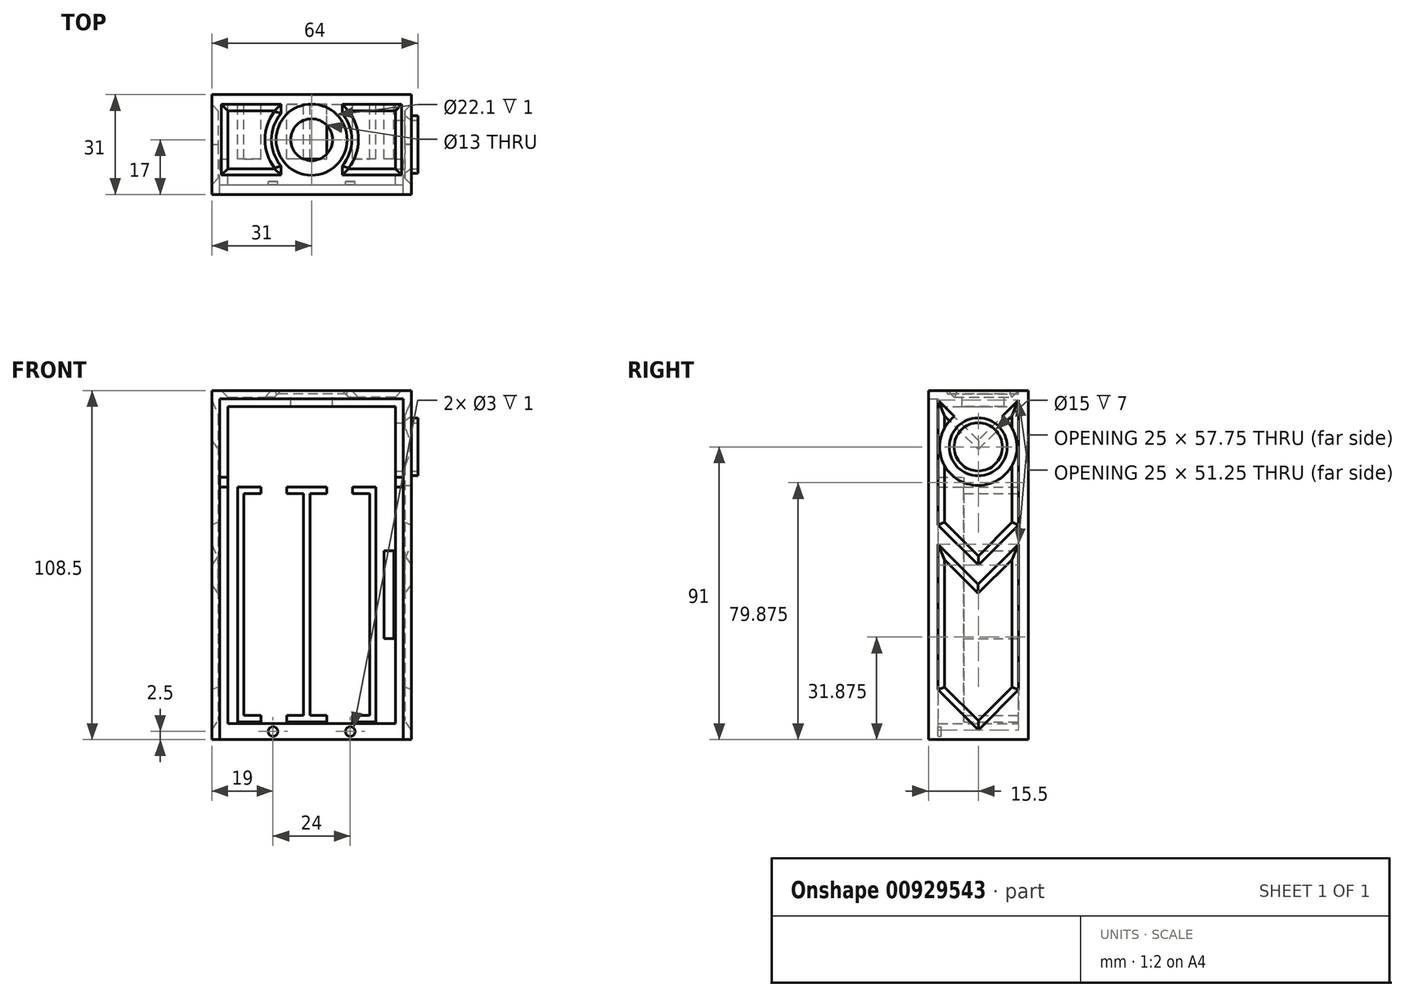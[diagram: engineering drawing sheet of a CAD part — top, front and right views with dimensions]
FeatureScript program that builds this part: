
annotation { "Feature Type Name" : "Feature", "Feature Type Description" : "" }
export const myFeature = defineFeature(function(context is Context, id is Id, definition is map)
    precondition{}
    {
        {
            var Q0;
            Q0=qCreatedBy(makeId("Front.planeOp"),FACE);
            var sketch = newSketch(context, id + "F0", { "sketchPlane" : qUnion([Q0])});
            skLineSegment(sketch, "E0.bottom", {"start": v(21.5, -36.5) * mm, "end": v(14.25, -36.5) * mm});
            skLineSegment(sketch, "E0.top", {"start": v(21.5, 36.5) * mm, "end": v(14.25, 36.5) * mm});
            skLineSegment(sketch, "E0.left", {"start": v(21.5, -36.5) * mm, "end": v(21.5, 36.5) * mm});
            skLineSegment(sketch, "E0.right", {"start": v(-21.5, -36.5) * mm, "end": v(-21.5, 36.5) * mm});
            skPoint(sketch, "E0.middle", {"position": v(0, 0) * mm});
            skLineSegment(sketch, "E1.bottom", {"start": v(-19.5, 34.5) * mm, "end": v(-14.25, 34.5) * mm});
            skLineSegment(sketch, "E1.top", {"start": v(-19.5, -34.5) * mm, "end": v(-14.25, -34.5) * mm});
            skLineSegment(sketch, "E1.left", {"start": v(-19.5, 34.5) * mm, "end": v(-19.5, -34.5) * mm});
            skLineSegment(sketch, "E1.right", {"start": v(-1, 34.5) * mm, "end": v(-1, -34.5) * mm});
            skLineSegment(sketch, "E2.bottom", {"start": v(1, 34.5) * mm, "end": v(6.25, 34.5) * mm});
            skLineSegment(sketch, "E2.top", {"start": v(1, -34.5) * mm, "end": v(6.25, -34.5) * mm});
            skLineSegment(sketch, "E2.left", {"start": v(1, 34.5) * mm, "end": v(1, -34.5) * mm});
            skLineSegment(sketch, "E2.right", {"start": v(19.5, 34.5) * mm, "end": v(19.5, -34.5) * mm});
            skLineSegment(sketch, "E3", {"start": v(-14.25, 34.5) * mm, "end": v(-14.25, 36.5) * mm});
            skLineSegment(sketch, "E4", {"start": v(-6.25, 34.5) * mm, "end": v(-6.25, 36.5) * mm});
            skLineSegment(sketch, "E5", {"start": v(6.25, 34.5) * mm, "end": v(6.25, 36.5) * mm});
            skLineSegment(sketch, "E6", {"start": v(14.25, 34.5) * mm, "end": v(14.25, 36.5) * mm});
            skLineSegment(sketch, "E7.trimOffspring", {"start": v(-6.25, 34.5) * mm, "end": v(-1, 34.5) * mm});
            skLineSegment(sketch, "E8.trimOffspring", {"start": v(-14.25, 36.5) * mm, "end": v(-21.5, 36.5) * mm});
            skLineSegment(sketch, "E9.trimOffspring", {"start": v(14.25, 34.5) * mm, "end": v(19.5, 34.5) * mm});
            skLineSegment(sketch, "E10.trimOffspring", {"start": v(6.25, 36.5) * mm, "end": v(-6.25, 36.5) * mm});
            skLineSegment(sketch, "E11", {"start": v(-14.25, -36.5) * mm, "end": v(-14.25, -34.5) * mm});
            skLineSegment(sketch, "E12", {"start": v(-6.25, -36.5) * mm, "end": v(-6.25, -34.5) * mm});
            skLineSegment(sketch, "E13.trimOffspring", {"start": v(-14.25, -36.5) * mm, "end": v(-21.5, -36.5) * mm});
            skLineSegment(sketch, "E14.trimOffspring", {"start": v(-6.25, -34.5) * mm, "end": v(-1, -34.5) * mm});
            skLineSegment(sketch, "E15", {"start": v(6.25, -34.5) * mm, "end": v(6.25, -36.5) * mm});
            skLineSegment(sketch, "E16", {"start": v(14.25, -34.5) * mm, "end": v(14.25, -36.5) * mm});
            skLineSegment(sketch, "E17.trimOffspring", {"start": v(6.25, -36.5) * mm, "end": v(-6.25, -36.5) * mm});
            skLineSegment(sketch, "E18.trimOffspring", {"start": v(14.25, -34.5) * mm, "end": v(19.5, -34.5) * mm});
            skLineSegment(sketch, "E19", {"start": v(-14.25, 36.5) * mm, "end": v(-6.25, 36.5) * mm});
            skLineSegment(sketch, "E20", {"start": v(-6.25, 34.5) * mm, "end": v(-14.25, 34.5) * mm});
            skLineSegment(sketch, "E21", {"start": v(6.25, 36.5) * mm, "end": v(14.25, 36.5) * mm});
            skLineSegment(sketch, "E22", {"start": v(14.25, 34.5) * mm, "end": v(6.25, 34.5) * mm});
            skSolve(sketch);
        }
        {
            var Q0;
            Q0=qCreatedBy(makeId("Front.planeOp"),FACE);
            var sketch = newSketch(context, id + "F1", { "sketchPlane" : qUnion([Q0])});
            skLineSegment(sketch, "E23.top", {"start": v(-24.5, -37) * mm, "end": v(27.5, -37) * mm});
            skLineSegment(sketch, "E23.left", {"start": v(-24.5, 36.5) * mm, "end": v(-24.5, -37) * mm});
            skLineSegment(sketch, "E23.right", {"start": v(27.5, 36.5) * mm, "end": v(27.5, -37) * mm});
            skLineSegment(sketch, "E24.top", {"start": v(-29.5, -42) * mm, "end": v(32.5, -42) * mm});
            skLineSegment(sketch, "E24.left", {"start": v(-29.5, 39.5) * mm, "end": v(-29.5, -42) * mm});
            skLineSegment(sketch, "E24.right", {"start": v(32.5, 39.5) * mm, "end": v(32.5, -42) * mm});
            skLineSegment(sketch, "E25", {"start": v(4, 39.5) * mm, "end": v(4, 39.5) * mm});
            skLineSegment(sketch, "E26.bottom", {"start": v(-27, 36.5) * mm, "end": v(-24.5, 36.5) * mm});
            skLineSegment(sketch, "E26.top", {"start": v(-27, 39.5) * mm, "end": v(-24.5, 39.5) * mm});
            skLineSegment(sketch, "E26.left", {"start": v(-27, 36.5) * mm, "end": v(-27, 39.5) * mm});
            skLineSegment(sketch, "E26.right", {"start": v(30, 36.5) * mm, "end": v(30, 39.5) * mm});
            skLineSegment(sketch, "E27.top", {"start": v(-29.5, 66.5) * mm, "end": v(32.5, 66.5) * mm});
            skLineSegment(sketch, "E27.left", {"start": v(-29.5, 39.5) * mm, "end": v(-29.5, 66.5) * mm});
            skLineSegment(sketch, "E27.right", {"start": v(32.5, 39.5) * mm, "end": v(32.5, 66.5) * mm});
            skLineSegment(sketch, "E28.top", {"start": v(-24.5, 61.5) * mm, "end": v(27.5, 61.5) * mm});
            skLineSegment(sketch, "E28.left", {"start": v(-24.5, 39.5) * mm, "end": v(-24.5, 61.5) * mm});
            skLineSegment(sketch, "E28.right", {"start": v(27.5, 39.5) * mm, "end": v(27.5, 61.5) * mm});
            skLineSegment(sketch, "E29.trimOffspring", {"start": v(27.5, 39.5) * mm, "end": v(30, 39.5) * mm});
            skPoint(sketch, "E30.orphan", {"position": v(4, 36.5) * mm});
            skPoint(sketch, "E31.end.orphan", {"position": v(-4, 39.5) * mm});
            skLineSegment(sketch, "E32.trimOffspring", {"start": v(27.5, 36.5) * mm, "end": v(30, 36.5) * mm});
            skLineSegment(sketch, "E33", {"start": v(-24.5, 39.5) * mm, "end": v(-24.5, 36.5) * mm});
            skLineSegment(sketch, "E34", {"start": v(27.5, 39.5) * mm, "end": v(27.5, 36.5) * mm});
            skLineSegment(sketch, "E35.left", {"start": v(-24.5, 61.5) * mm, "end": v(-24.5, -37) * mm});
            skLineSegment(sketch, "E35.right", {"start": v(27.5, 61.5) * mm, "end": v(27.5, -37) * mm});
            skLineSegment(sketch, "E36.bottom", {"start": v(21.5, -36.5) * mm, "end": v(14.25, -36.5) * mm});
            skLineSegment(sketch, "E36.top", {"start": v(21.5, 36.5) * mm, "end": v(14.25, 36.5) * mm});
            skLineSegment(sketch, "E36.left", {"start": v(21.5, -36.5) * mm, "end": v(21.5, 36.5) * mm});
            skLineSegment(sketch, "E36.right", {"start": v(-21.5, -36.5) * mm, "end": v(-21.5, 36.5) * mm});
            skPoint(sketch, "E36.middle", {"position": v(0, 0) * mm});
            skLineSegment(sketch, "E37.bottom", {"start": v(-19.5, 34.5) * mm, "end": v(-14.25, 34.5) * mm});
            skLineSegment(sketch, "E37.top", {"start": v(-19.5, -34.5) * mm, "end": v(-14.25, -34.5) * mm});
            skLineSegment(sketch, "E37.left", {"start": v(-19.5, 34.5) * mm, "end": v(-19.5, -34.5) * mm});
            skLineSegment(sketch, "E37.right", {"start": v(-1, 34.5) * mm, "end": v(-1, -34.5) * mm});
            skLineSegment(sketch, "E38.bottom", {"start": v(1, 34.5) * mm, "end": v(6.25, 34.5) * mm});
            skLineSegment(sketch, "E38.top", {"start": v(1, -34.5) * mm, "end": v(6.25, -34.5) * mm});
            skLineSegment(sketch, "E38.left", {"start": v(1, 34.5) * mm, "end": v(1, -34.5) * mm});
            skLineSegment(sketch, "E38.right", {"start": v(19.5, 34.5) * mm, "end": v(19.5, -34.5) * mm});
            skLineSegment(sketch, "E39", {"start": v(-14.25, 34.5) * mm, "end": v(-14.25, 36.5) * mm});
            skLineSegment(sketch, "E40", {"start": v(-6.25, 34.5) * mm, "end": v(-6.25, 36.5) * mm});
            skLineSegment(sketch, "E41", {"start": v(6.25, 34.5) * mm, "end": v(6.25, 36.5) * mm});
            skLineSegment(sketch, "E42", {"start": v(14.25, 34.5) * mm, "end": v(14.25, 36.5) * mm});
            skLineSegment(sketch, "E43.trimOffspring", {"start": v(-6.25, 34.5) * mm, "end": v(-1, 34.5) * mm});
            skLineSegment(sketch, "E44.trimOffspring", {"start": v(-14.25, 36.5) * mm, "end": v(-21.5, 36.5) * mm});
            skLineSegment(sketch, "E45.trimOffspring", {"start": v(14.25, 34.5) * mm, "end": v(19.5, 34.5) * mm});
            skLineSegment(sketch, "E46.trimOffspring", {"start": v(6.25, 36.5) * mm, "end": v(-6.25, 36.5) * mm});
            skLineSegment(sketch, "E47", {"start": v(-14.25, -36.5) * mm, "end": v(-14.25, -34.5) * mm});
            skLineSegment(sketch, "E48", {"start": v(-6.25, -36.5) * mm, "end": v(-6.25, -34.5) * mm});
            skLineSegment(sketch, "E49.trimOffspring", {"start": v(-14.25, -36.5) * mm, "end": v(-21.5, -36.5) * mm});
            skLineSegment(sketch, "E50.trimOffspring", {"start": v(-6.25, -34.5) * mm, "end": v(-1, -34.5) * mm});
            skLineSegment(sketch, "E51", {"start": v(6.25, -34.5) * mm, "end": v(6.25, -36.5) * mm});
            skLineSegment(sketch, "E52", {"start": v(14.25, -34.5) * mm, "end": v(14.25, -36.5) * mm});
            skLineSegment(sketch, "E53.trimOffspring", {"start": v(6.25, -36.5) * mm, "end": v(-6.25, -36.5) * mm});
            skLineSegment(sketch, "E54.trimOffspring", {"start": v(14.25, -34.5) * mm, "end": v(19.5, -34.5) * mm});
            skPoint(sketch, "E28.bottom.start.orphan", {"position": v(-4, 36.5) * mm});
            skLineSegment(sketch, "E55.left", {"start": v(27.5, 16.72) * mm, "end": v(27.5, -10.62) * mm});
            skLineSegment(sketch, "E55.right", {"start": v(27, 16.72) * mm, "end": v(27, -10.62) * mm});
            skLineSegment(sketch, "E56.bottom", {"start": v(27, 16.72) * mm, "end": v(24, 16.72) * mm});
            skLineSegment(sketch, "E56.top", {"start": v(27, -10.62) * mm, "end": v(24, -10.62) * mm});
            skLineSegment(sketch, "E56.right", {"start": v(24, 16.72) * mm, "end": v(24, -10.62) * mm});
            skLineSegment(sketch, "E57", {"start": v(-27, 64) * mm, "end": v(30, 64) * mm});
            skLineSegment(sketch, "E58", {"start": v(-27, 64) * mm, "end": v(-27, -42) * mm});
            skLineSegment(sketch, "E59", {"start": v(30, -42) * mm, "end": v(30, 64) * mm});
            skCircle(sketch, "E60", {"center": v(-10.5, -39.5) * mm, "radius": 1.5 * mm});
            skCircle(sketch, "E61", {"center": v(13.5, -39.5) * mm, "radius": 1.5 * mm});
            skSolve(sketch);
        }
        {
            var Q0;
            {var subQ4=sQuery(id+"F1.wireOp",EDGE,"E24.left");Q0=makeQuery(id+"F1.imprint","IMPRINT",FACE,{"disambiguationData":[TD([[makeQuery(id+"F1.imprint","IMPRINT",EDGE,{"derivedFrom":subQ4}),1.0]])]});}
            extrude(context, id + "F2", {"entities" : qUnion([Q0]), "depth" : 31 * mm, "offsetDistance" : 25 * mm});
        }
        {
            var Q0;
            {var subQ0=sQuery(id+"F1.wireOp",EDGE,"E26.bottom");Q0=makeQuery(id+"F1.imprint","IMPRINT",FACE,{"disambiguationData":[TD([[makeQuery(id+"F1.imprint","IMPRINT",EDGE,{"derivedFrom":subQ0}),1.0]])]});}
            var Q1;
            {var subQ0=sQuery(id+"F1.wireOp",EDGE,"E29.trimOffspring");Q1=makeQuery(id+"F1.imprint","IMPRINT",FACE,{"disambiguationData":[TD([[makeQuery(id+"F1.imprint","IMPRINT",EDGE,{"derivedFrom":subQ0}),-1.0]])]});}
            extrude(context, id + "F3", {"entities" : qUnion([Q0, Q1]), "operationType" : NewBodyOperationType.ADD, "depth" : 20 * mm, "offsetDistance" : 25 * mm});
        }
        {
            var Q0;
            {var subQ3=sQuery(id+"F1.wireOp",EDGE,"E28.top");Q0=makeQuery(id+"F1.imprint","IMPRINT",FACE,{"disambiguationData":[TD([[makeQuery(id+"F1.imprint","IMPRINT",EDGE,{"derivedFrom":subQ3}),-1.0]])]});}
            extrude(context, id + "F4", {"entities" : qUnion([Q0]), "operationType" : NewBodyOperationType.ADD, "depth" : 3 * mm, "offsetDistance" : 25 * mm});
        }
        {
            var Q0;
            Q0=makeQuery(id+"F1.imprint","IMPRINT",FACE,{"disambiguationData":[TD([[makeQuery(id+"F1.imprint","IMPRINT",EDGE,{"derivedFrom":sQuery(id+"F1.wireOp",EDGE,"E36.right")}),-1.0]])]});
            var Q1;
            Q1=makeQuery(id+"F1.imprint","IMPRINT",FACE,{"disambiguationData":[TD([[makeQuery(id+"F1.imprint","IMPRINT",EDGE,{"derivedFrom":sQuery(id+"F1.wireOp",EDGE,"E37.right")}),1.0]])]});
            var Q2;
            Q2=makeQuery(id+"F1.imprint","IMPRINT",FACE,{"disambiguationData":[TD([[makeQuery(id+"F1.imprint","IMPRINT",EDGE,{"derivedFrom":sQuery(id+"F1.wireOp",EDGE,"E36.bottom")}),-1.0]])]});
            var Q3;
            Q3=makeQuery(id+"F1.imprint","IMPRINT",FACE,{"disambiguationData":[TD([[makeQuery(id+"F1.imprint","IMPRINT",EDGE,{"derivedFrom":sQuery(id+"F1.wireOp",EDGE,"E56.bottom")}),1.0]])]});
            extrude(context, id + "F5", {"entities" : qUnion([Q0, Q1, Q2, Q3]), "operationType" : NewBodyOperationType.ADD, "depth" : 20 * mm, "offsetDistance" : 25 * mm});
        }
        {
            var Q0;
            {var subQ1=sQuery(id+"F1.wireOp",EDGE,"E26.top");Q0=makeQuery(id+"F1.imprint","IMPRINT",FACE,{"disambiguationData":[TD([[makeQuery(id+"F1.imprint","IMPRINT",EDGE,{"derivedFrom":subQ1}),1.0]])]});}
            var Q1;
            {var subQ9=sQuery(id+"F1.wireOp",EDGE,"E26.bottom");Q1=makeQuery(id+"F1.imprint","IMPRINT",FACE,{"disambiguationData":[TD([[makeQuery(id+"F1.imprint","IMPRINT",EDGE,{"derivedFrom":subQ9}),-1.0]])]});}
            extrude(context, id + "F6", {"entities" : qUnion([Q0, Q1]), "operationType" : NewBodyOperationType.ADD, "depth" : 28 * mm, "offsetDistance" : 25 * mm});
        }
        {
            var Q0;
            Q0=makeQuery(id+"F1.imprint","IMPRINT",FACE,{"disambiguationData":[TD([[makeQuery(id+"F1.imprint","IMPRINT",EDGE,{"derivedFrom":sQuery(id+"F1.wireOp",EDGE,"E60")}),1.0]])]});
            var Q1;
            Q1=makeQuery(id+"F1.imprint","IMPRINT",FACE,{"disambiguationData":[TD([[makeQuery(id+"F1.imprint","IMPRINT",EDGE,{"derivedFrom":sQuery(id+"F1.wireOp",EDGE,"E61")}),1.0]])]});
            extrude(context, id + "F7", {"entities" : qUnion([Q0, Q1]), "operationType" : NewBodyOperationType.ADD, "depth" : 27 * mm, "offsetDistance" : 25 * mm});
        }
        {
            var Q0;
            Q0=makeQuery(id+"F2.opExtrude","SWEPT_FACE",FACE,{"disambiguationData":[OSD([sQuery(id+"F1.wireOp",EDGE,"E27.top")])]});
            var sketch = newSketch(context, id + "F8", { "sketchPlane" : qUnion([Q0])});
            skLineSegment(sketch, "E62.bottom", {"start": v(-29.5, 0) * mm, "end": v(32.5, 0) * mm});
            skLineSegment(sketch, "E62.top", {"start": v(-29.5, -28) * mm, "end": v(32.5, -28) * mm});
            skLineSegment(sketch, "E62.left", {"start": v(-29.5, 0) * mm, "end": v(-29.5, -28) * mm});
            skLineSegment(sketch, "E62.right", {"start": v(32.5, 0) * mm, "end": v(32.5, -28) * mm});
            skLineSegment(sketch, "E63", {"start": v(-29.5, -14) * mm, "end": v(32.5, -14) * mm});
            skLineSegment(sketch, "E64", {"start": v(1.5, 0) * mm, "end": v(1.5, -28) * mm});
            skCircle(sketch, "E65", {"center": v(1.5, -14) * mm, "radius": 11.05 * mm});
            skCircle(sketch, "E66", {"center": v(1.5, -14) * mm, "radius": 6.5 * mm});
            skLineSegment(sketch, "E67.bottom", {"start": v(-26.5, -3) * mm, "end": v(-8, -3) * mm});
            skLineSegment(sketch, "E67.top", {"start": v(-26.5, -25) * mm, "end": v(-8, -25) * mm});
            skLineSegment(sketch, "E67.left", {"start": v(-26.5, -3) * mm, "end": v(-26.5, -25) * mm});
            skLineSegment(sketch, "E67.right", {"start": v(-8, -3) * mm, "end": v(-8, -25) * mm});
            skCircle(sketch, "E68", {"center": v(1.5, -14) * mm, "radius": 12.5 * mm});
            skLineSegment(sketch, "E69.bottom", {"start": v(11, -3) * mm, "end": v(29.5, -3) * mm});
            skLineSegment(sketch, "E69.top", {"start": v(11, -25) * mm, "end": v(29.5, -25) * mm});
            skLineSegment(sketch, "E69.left", {"start": v(11, -3) * mm, "end": v(11, -25) * mm});
            skLineSegment(sketch, "E69.right", {"start": v(29.5, -3) * mm, "end": v(29.5, -25) * mm});
            skSolve(sketch);
        }
        {
            var Q0;
            {var subQ0=sQuery(id+"F8.wireOp",EDGE,"E66");var subQ1=sQuery(id+"F8.wireOp",EDGE,"E63");var subQ2=makeQuery(id+"F8.imprint","INTERSECT",VERTEX,{"disambiguationData":[OD(1.0)],"derivedFrom":[subQ1,subQ0]});Q0=makeQuery(id+"F8.imprint","IMPRINT",FACE,{"disambiguationData":[TD([[makeQuery(id+"F8.imprint","IMPRINT",EDGE,{"disambiguationData":[TD([[subQ2,-1.0]])],"derivedFrom":subQ1}),-1.0]])]});}
            var Q1;
            {var subQ0=sQuery(id+"F8.wireOp",EDGE,"E65");var subQ1=sQuery(id+"F8.wireOp",EDGE,"E63");var subQ2=makeQuery(id+"F8.imprint","INTERSECT",VERTEX,{"disambiguationData":[OD(0.0)],"derivedFrom":[subQ1,subQ0]});Q1=makeQuery(id+"F8.imprint","IMPRINT",FACE,{"disambiguationData":[TD([[makeQuery(id+"F8.imprint","IMPRINT",EDGE,{"disambiguationData":[TD([[subQ2,-1.0]])],"derivedFrom":subQ1}),-1.0]])]});}
            var Q2;
            {var subQ0=sQuery(id+"F8.wireOp",EDGE,"E65");var subQ1=sQuery(id+"F8.wireOp",EDGE,"E63");var subQ2=makeQuery(id+"F8.imprint","INTERSECT",VERTEX,{"disambiguationData":[OD(0.0)],"derivedFrom":[subQ1,subQ0]});Q2=makeQuery(id+"F8.imprint","IMPRINT",FACE,{"disambiguationData":[TD([[makeQuery(id+"F8.imprint","IMPRINT",EDGE,{"disambiguationData":[TD([[subQ2,-1.0]])],"derivedFrom":subQ1}),1.0]])]});}
            var Q3;
            {var subQ0=sQuery(id+"F8.wireOp",EDGE,"E66");var subQ1=sQuery(id+"F8.wireOp",EDGE,"E63");var subQ2=makeQuery(id+"F8.imprint","INTERSECT",VERTEX,{"disambiguationData":[OD(1.0)],"derivedFrom":[subQ1,subQ0]});Q3=makeQuery(id+"F8.imprint","IMPRINT",FACE,{"disambiguationData":[TD([[makeQuery(id+"F8.imprint","IMPRINT",EDGE,{"disambiguationData":[TD([[subQ2,-1.0]])],"derivedFrom":subQ1}),1.0]])]});}
            var Q4;
            {var subQ1=sQuery(id+"F8.wireOp",EDGE,"E63");var subQ7=sQuery(id+"F8.wireOp",EDGE,"E67.right");var subQ9=makeQuery(id+"F8.imprint","INTERSECT",VERTEX,{"derivedFrom":[subQ1,subQ7]});Q4=makeQuery(id+"F8.imprint","IMPRINT",FACE,{"disambiguationData":[TD([[makeQuery(id+"F8.imprint","IMPRINT",EDGE,{"disambiguationData":[TD([[subQ9,-1.0]])],"derivedFrom":subQ1}),-1.0]])]});}
            var Q5;
            {var subQ3=sQuery(id+"F8.wireOp",EDGE,"E67.right");var subQ6=sQuery(id+"F8.wireOp",EDGE,"E63");var subQ9=makeQuery(id+"F8.imprint","INTERSECT",VERTEX,{"derivedFrom":[subQ6,subQ3]});Q5=makeQuery(id+"F8.imprint","IMPRINT",FACE,{"disambiguationData":[TD([[makeQuery(id+"F8.imprint","IMPRINT",EDGE,{"disambiguationData":[TD([[subQ9,-1.0]])],"derivedFrom":subQ6}),1.0]])]});}
            var Q6;
            {var subQ0=sQuery(id+"F8.wireOp",EDGE,"E69.left");var subQ1=sQuery(id+"F8.wireOp",EDGE,"E63");var subQ2=makeQuery(id+"F8.imprint","INTERSECT",VERTEX,{"derivedFrom":[subQ1,subQ0]});Q6=makeQuery(id+"F8.imprint","IMPRINT",FACE,{"disambiguationData":[TD([[makeQuery(id+"F8.imprint","IMPRINT",EDGE,{"disambiguationData":[TD([[subQ2,-1.0]])],"derivedFrom":subQ1}),1.0]])]});}
            var Q7;
            {var subQ0=sQuery(id+"F8.wireOp",EDGE,"E69.left");var subQ1=sQuery(id+"F8.wireOp",EDGE,"E63");var subQ2=makeQuery(id+"F8.imprint","INTERSECT",VERTEX,{"derivedFrom":[subQ1,subQ0]});Q7=makeQuery(id+"F8.imprint","IMPRINT",FACE,{"disambiguationData":[TD([[makeQuery(id+"F8.imprint","IMPRINT",EDGE,{"disambiguationData":[TD([[subQ2,-1.0]])],"derivedFrom":subQ1}),-1.0]])]});}
            extrude(context, id + "F9", {"entities" : qUnion([Q0, Q1, Q2, Q3, Q4, Q5, Q6, Q7]), "operationType" : NewBodyOperationType.REMOVE, "oppositeDirection" : true, "depth" : 1 * mm, "offsetDistance" : 25 * mm});
        }
        {
            var Q0;
            {var subQ0=sQuery(id+"F8.wireOp",EDGE,"E64");var subQ1=sQuery(id+"F8.wireOp",EDGE,"E63");var subQ2=makeQuery(id+"F8.imprint","INTERSECT",VERTEX,{"derivedFrom":[subQ1,subQ0]});Q0=makeQuery(id+"F8.imprint","IMPRINT",FACE,{"disambiguationData":[TD([[makeQuery(id+"F8.imprint","IMPRINT",EDGE,{"disambiguationData":[TD([[subQ2,-1.0]])],"derivedFrom":subQ1}),-1.0]])]});}
            var Q1;
            {var subQ0=sQuery(id+"F8.wireOp",EDGE,"E66");var subQ1=sQuery(id+"F8.wireOp",EDGE,"E63");var subQ2=makeQuery(id+"F8.imprint","INTERSECT",VERTEX,{"disambiguationData":[OD(0.0)],"derivedFrom":[subQ1,subQ0]});Q1=makeQuery(id+"F8.imprint","IMPRINT",FACE,{"disambiguationData":[TD([[makeQuery(id+"F8.imprint","IMPRINT",EDGE,{"disambiguationData":[TD([[subQ2,-1.0]])],"derivedFrom":subQ1}),1.0]])]});}
            var Q2;
            {var subQ0=sQuery(id+"F8.wireOp",EDGE,"E64");var subQ1=sQuery(id+"F8.wireOp",EDGE,"E63");var subQ2=makeQuery(id+"F8.imprint","INTERSECT",VERTEX,{"derivedFrom":[subQ1,subQ0]});Q2=makeQuery(id+"F8.imprint","IMPRINT",FACE,{"disambiguationData":[TD([[makeQuery(id+"F8.imprint","IMPRINT",EDGE,{"disambiguationData":[TD([[subQ2,-1.0]])],"derivedFrom":subQ1}),1.0]])]});}
            var Q3;
            {var subQ0=sQuery(id+"F8.wireOp",EDGE,"E66");var subQ1=sQuery(id+"F8.wireOp",EDGE,"E63");var subQ2=makeQuery(id+"F8.imprint","INTERSECT",VERTEX,{"disambiguationData":[OD(0.0)],"derivedFrom":[subQ1,subQ0]});Q3=makeQuery(id+"F8.imprint","IMPRINT",FACE,{"disambiguationData":[TD([[makeQuery(id+"F8.imprint","IMPRINT",EDGE,{"disambiguationData":[TD([[subQ2,-1.0]])],"derivedFrom":subQ1}),-1.0]])]});}
            extrude(context, id + "F10", {"entities" : qUnion([Q0, Q1, Q2, Q3]), "operationType" : NewBodyOperationType.REMOVE, "oppositeDirection" : true, "depth" : 5 * mm, "offsetDistance" : 25 * mm});
        }
        {
            var Q0;
            Q0=makeQuery(id+"F2.opExtrude","SWEPT_FACE",FACE,{"disambiguationData":[OSD([sQuery(id+"F1.wireOp",EDGE,"E24.right"),sQuery(id+"F1.wireOp",EDGE,"E27.right")])]});
            var sketch = newSketch(context, id + "F11", { "sketchPlane" : qUnion([Q0])});
            skLineSegment(sketch, "E70.bottom", {"start": v(-31, 66.5) * mm, "end": v(0, 66.5) * mm});
            skLineSegment(sketch, "E70.top", {"start": v(-31, 61.5) * mm, "end": v(0, 61.5) * mm});
            skLineSegment(sketch, "E70.left", {"start": v(-31, 66.5) * mm, "end": v(-31, 61.5) * mm});
            skLineSegment(sketch, "E70.right", {"start": v(0, 66.5) * mm, "end": v(0, 61.5) * mm});
            skLineSegment(sketch, "E71.top", {"start": v(-31, 36.5) * mm, "end": v(0, 36.5) * mm});
            skLineSegment(sketch, "E71.left", {"start": v(-31, 61.5) * mm, "end": v(-31, 36.5) * mm});
            skLineSegment(sketch, "E71.right", {"start": v(0, 61.5) * mm, "end": v(0, 36.5) * mm});
            skCircle(sketch, "E72", {"center": v(-15.5, 49) * mm, "radius": 7.5 * mm});
            skPoint(sketch, "E72.centerSnap0", {"position": v(0, 49) * mm});
            skPoint(sketch, "E72.centerSnap1", {"position": v(-15.5, 61.5) * mm});
            skCircle(sketch, "E73", {"center": v(-15.5, 49) * mm, "radius": 9 * mm});
            skLineSegment(sketch, "E74.top", {"start": v(-31.06, -42) * mm, "end": v(0, -42) * mm});
            skLineSegment(sketch, "E74.left", {"start": v(-31.06, 65.12) * mm, "end": v(-31.06, -42) * mm});
            skLineSegment(sketch, "E74.right", {"start": v(0, 65.12) * mm, "end": v(0, -42) * mm});
            skLineSegment(sketch, "E75", {"start": v(-31, 12.25) * mm, "end": v(0, 12.25) * mm});
            skLineSegment(sketch, "E76", {"start": v(-15.53, -42) * mm, "end": v(-15.53, 66.5) * mm});
            skPoint(sketch, "E76.endSnap0", {"position": v(-15.5, 66.5) * mm});
            skLineSegment(sketch, "E77.bottom", {"start": v(-3, -39) * mm, "end": v(-28, -39) * mm});
            skLineSegment(sketch, "E77.top", {"start": v(-3, 63.5) * mm, "end": v(-28, 63.5) * mm});
            skLineSegment(sketch, "E77.left", {"start": v(-3, -39) * mm, "end": v(-3, 63.5) * mm});
            skLineSegment(sketch, "E77.right", {"start": v(-28, -39) * mm, "end": v(-28, 63.5) * mm});
            skPoint(sketch, "E77.middle", {"position": v(-15.5, 12.25) * mm});
            skLineSegment(sketch, "E78", {"start": v(-15.5, 12.25) * mm, "end": v(-3, 24.75) * mm});
            skLineSegment(sketch, "E79", {"start": v(-15.5, 12.25) * mm, "end": v(-28, 24.75) * mm});
            skLineSegment(sketch, "E80", {"start": v(-15.53, 6.25) * mm, "end": v(-3, 18.75) * mm});
            skLineSegment(sketch, "E81", {"start": v(-15.53, 6.25) * mm, "end": v(-28, 18.75) * mm});
            skLineSegment(sketch, "E82", {"start": v(-15.5, -39) * mm, "end": v(-3, -26.5) * mm});
            skLineSegment(sketch, "E83", {"start": v(-15.5, -39) * mm, "end": v(-28, -26.5) * mm});
            skCircle(sketch, "E84", {"center": v(-15.5, 49) * mm, "radius": 12 * mm});
            skLineSegment(sketch, "E85", {"start": v(-3, 63.5) * mm, "end": v(-15.53, 50.97) * mm});
            skLineSegment(sketch, "E86", {"start": v(-28, 63.5) * mm, "end": v(-15.53, 50.97) * mm});
            skSolve(sketch);
        }
        {
            var Q0;
            Q0=makeQuery(id+"F11.imprint","IMPRINT",FACE,{"disambiguationData":[TD([[makeQuery(id+"F11.imprint","IMPRINT",EDGE,{"derivedFrom":sQuery(id+"F11.wireOp",EDGE,"E72")}),1.0]])]});
            var Q1;
            Q1=sQuery(id+"F11.wireOp",EDGE,"E72");
            extrude(context, id + "F12", {"entities" : qUnion([Q0]), "operationType" : NewBodyOperationType.REMOVE, "surfaceEntities" : qUnion([Q1]), "oppositeDirection" : true, "depth" : 5 * mm, "offsetDistance" : 25 * mm});
        }
        {
            var Q0;
            Q0=makeQuery(id+"F11.imprint","IMPRINT",FACE,{"disambiguationData":[TD([[makeQuery(id+"F11.imprint","IMPRINT",EDGE,{"derivedFrom":sQuery(id+"F11.wireOp",EDGE,"E72")}),-1.0]])]});
            extrude(context, id + "F13", {"entities" : qUnion([Q0]), "operationType" : NewBodyOperationType.ADD, "depth" : 2 * mm, "offsetDistance" : 25 * mm});
        }
        {
            var Q0;
            {var subQ1=sQuery(id+"F8.wireOp",EDGE,"E67.top");Q0=makeQuery(id+"F8.imprint","IMPRINT",FACE,{"disambiguationData":[TD([[makeQuery(id+"F8.imprint","IMPRINT",EDGE,{"derivedFrom":subQ1}),1.0]])]});}
            var Q1;
            {var subQ1=sQuery(id+"F8.wireOp",EDGE,"E67.bottom");Q1=makeQuery(id+"F8.imprint","IMPRINT",FACE,{"disambiguationData":[TD([[makeQuery(id+"F8.imprint","IMPRINT",EDGE,{"derivedFrom":subQ1}),-1.0]])]});}
            var Q2;
            {var subQ1=sQuery(id+"F8.wireOp",EDGE,"E69.top");Q2=makeQuery(id+"F8.imprint","IMPRINT",FACE,{"disambiguationData":[TD([[makeQuery(id+"F8.imprint","IMPRINT",EDGE,{"derivedFrom":subQ1}),1.0]])]});}
            var Q3;
            {var subQ1=sQuery(id+"F8.wireOp",EDGE,"E69.bottom");Q3=makeQuery(id+"F8.imprint","IMPRINT",FACE,{"disambiguationData":[TD([[makeQuery(id+"F8.imprint","IMPRINT",EDGE,{"derivedFrom":subQ1}),-1.0]])]});}
            extrude(context, id + "F14", {"entities" : qUnion([Q0, Q1, Q2, Q3]), "operationType" : NewBodyOperationType.REMOVE, "oppositeDirection" : true, "depth" : 2 * mm, "offsetDistance" : 25 * mm});
        }
        {
            var Q0;
            Q0=makeQuery(id+"F14.boolean.opBoolean","COPY",EDGE,{"derivedFrom":makeQuery(id+"F14.opExtrude","CAP_EDGE",EDGE,{"disambiguationData":[OSD([sQuery(id+"F8.wireOp",EDGE,"E67.bottom")])],"isStart":false})});
            var Q1;
            Q1=makeQuery(id+"F14.boolean.opBoolean","COPY",EDGE,{"derivedFrom":makeQuery(id+"F14.opExtrude","CAP_EDGE",EDGE,{"disambiguationData":[OSD([sQuery(id+"F8.wireOp",EDGE,"E67.left")])],"isStart":false})});
            var Q2;
            Q2=makeQuery(id+"F14.boolean.opBoolean","COPY",EDGE,{"derivedFrom":makeQuery(id+"F14.opExtrude","CAP_EDGE",EDGE,{"disambiguationData":[OSD([sQuery(id+"F8.wireOp",EDGE,"E67.top")])],"isStart":false})});
            var Q3;
            {var subQ0=sQuery(id+"F8.wireOp",EDGE,"E68");var subQ1=makeQuery(id+"F8.imprint","INTERSECT",VERTEX,{"disambiguationData":[OD(0.0)],"derivedFrom":[sQuery(id+"F8.wireOp",EDGE,"E63"),subQ0]});Q3=makeQuery(id+"F14.boolean.opBoolean","COPY",EDGE,{"derivedFrom":makeQuery(id+"F14.opExtrude","CAP_EDGE",EDGE,{"disambiguationData":[OSD([subQ0]),TDD([makeQuery(id+"F8.imprint","IMPRINT",EDGE,{"disambiguationData":[TD([[subQ1,1.0]])],"derivedFrom":subQ0}),makeQuery(id+"F8.imprint","IMPRINT",EDGE,{"disambiguationData":[TD([[subQ1,-1.0]])],"derivedFrom":subQ0})])],"isStart":false})});}
            var Q4;
            {var subQ0=sQuery(id+"F8.wireOp",EDGE,"E67.right");Q4=makeQuery(id+"F14.boolean.opBoolean","COPY",EDGE,{"derivedFrom":makeQuery(id+"F14.opExtrude","CAP_EDGE",EDGE,{"disambiguationData":[OSD([subQ0]),TDD([makeQuery(id+"F8.imprint","IMPRINT",EDGE,{"disambiguationData":[TD([[makeQuery(id+"F8.imprint","INTERSECT",VERTEX,{"derivedFrom":[sQuery(id+"F8.wireOp",EDGE,"E67.bottom"),subQ0]}),-1.0]])],"derivedFrom":subQ0})])],"isStart":false})});}
            var Q5;
            {var subQ0=sQuery(id+"F8.wireOp",EDGE,"E67.right");Q5=makeQuery(id+"F14.boolean.opBoolean","COPY",EDGE,{"derivedFrom":makeQuery(id+"F14.opExtrude","CAP_EDGE",EDGE,{"disambiguationData":[OSD([subQ0]),TDD([makeQuery(id+"F8.imprint","IMPRINT",EDGE,{"disambiguationData":[TD([[makeQuery(id+"F8.imprint","INTERSECT",VERTEX,{"derivedFrom":[sQuery(id+"F8.wireOp",EDGE,"E67.top"),subQ0]}),1.0]])],"derivedFrom":subQ0})])],"isStart":false})});}
            var Q6;
            {var subQ0=sQuery(id+"F8.wireOp",EDGE,"E68");var subQ1=makeQuery(id+"F8.imprint","INTERSECT",VERTEX,{"disambiguationData":[OD(1.0)],"derivedFrom":[sQuery(id+"F8.wireOp",EDGE,"E63"),subQ0]});Q6=makeQuery(id+"F14.boolean.opBoolean","COPY",EDGE,{"derivedFrom":makeQuery(id+"F14.opExtrude","CAP_EDGE",EDGE,{"disambiguationData":[OSD([subQ0]),TDD([makeQuery(id+"F8.imprint","IMPRINT",EDGE,{"disambiguationData":[TD([[subQ1,-1.0]])],"derivedFrom":subQ0}),makeQuery(id+"F8.imprint","IMPRINT",EDGE,{"disambiguationData":[TD([[subQ1,1.0]])],"derivedFrom":subQ0})])],"isStart":false})});}
            var Q7;
            {var subQ0=sQuery(id+"F8.wireOp",EDGE,"E69.left");Q7=makeQuery(id+"F14.boolean.opBoolean","COPY",EDGE,{"derivedFrom":makeQuery(id+"F14.opExtrude","CAP_EDGE",EDGE,{"disambiguationData":[OSD([subQ0]),TDD([makeQuery(id+"F8.imprint","IMPRINT",EDGE,{"disambiguationData":[TD([[makeQuery(id+"F8.imprint","INTERSECT",VERTEX,{"derivedFrom":[sQuery(id+"F8.wireOp",EDGE,"E69.bottom"),subQ0]}),-1.0]])],"derivedFrom":subQ0})])],"isStart":false})});}
            var Q8;
            {var subQ0=sQuery(id+"F8.wireOp",EDGE,"E69.left");Q8=makeQuery(id+"F14.boolean.opBoolean","COPY",EDGE,{"derivedFrom":makeQuery(id+"F14.opExtrude","CAP_EDGE",EDGE,{"disambiguationData":[OSD([subQ0]),TDD([makeQuery(id+"F8.imprint","IMPRINT",EDGE,{"disambiguationData":[TD([[makeQuery(id+"F8.imprint","INTERSECT",VERTEX,{"derivedFrom":[sQuery(id+"F8.wireOp",EDGE,"E69.top"),subQ0]}),1.0]])],"derivedFrom":subQ0})])],"isStart":false})});}
            var Q9;
            Q9=makeQuery(id+"F14.boolean.opBoolean","COPY",EDGE,{"derivedFrom":makeQuery(id+"F14.opExtrude","CAP_EDGE",EDGE,{"disambiguationData":[OSD([sQuery(id+"F8.wireOp",EDGE,"E69.bottom")])],"isStart":false})});
            var Q10;
            Q10=makeQuery(id+"F14.boolean.opBoolean","COPY",EDGE,{"derivedFrom":makeQuery(id+"F14.opExtrude","CAP_EDGE",EDGE,{"disambiguationData":[OSD([sQuery(id+"F8.wireOp",EDGE,"E69.right")])],"isStart":false})});
            var Q11;
            Q11=makeQuery(id+"F14.boolean.opBoolean","COPY",EDGE,{"derivedFrom":makeQuery(id+"F14.opExtrude","CAP_EDGE",EDGE,{"disambiguationData":[OSD([sQuery(id+"F8.wireOp",EDGE,"E69.top")])],"isStart":false})});
            chamfer(context, id + "F15", {"entities" : qUnion([Q0, Q1, Q2, Q3, Q4, Q5, Q6, Q7, Q8, Q9, Q10, Q11]), "width" : 2 * mm, "tangentPropagation" : true});
        }
        {
            var Q0;
            Q0=makeQuery(id+"F2.opExtrude","SWEPT_FACE",FACE,{"disambiguationData":[OSD([sQuery(id+"F1.wireOp",EDGE,"E24.left"),sQuery(id+"F1.wireOp",EDGE,"E27.left")])]});
            var sketch = newSketch(context, id + "F16", { "sketchPlane" : qUnion([Q0])});
            skLineSegment(sketch, "E87.bottom", {"start": v(0, 66.5) * mm, "end": v(31, 66.5) * mm});
            skLineSegment(sketch, "E87.top", {"start": v(0, -42) * mm, "end": v(31, -42) * mm});
            skLineSegment(sketch, "E87.left", {"start": v(0, 66.5) * mm, "end": v(0, -42) * mm});
            skLineSegment(sketch, "E87.right", {"start": v(31, 66.5) * mm, "end": v(31, -42) * mm});
            skLineSegment(sketch, "E88.bottom", {"start": v(3, 63.5) * mm, "end": v(28, 63.5) * mm});
            skLineSegment(sketch, "E88.top", {"start": v(3, -39) * mm, "end": v(28, -39) * mm});
            skLineSegment(sketch, "E88.left", {"start": v(3, 63.5) * mm, "end": v(3, -39) * mm});
            skLineSegment(sketch, "E88.right", {"start": v(28, 63.5) * mm, "end": v(28, -39) * mm});
            skLineSegment(sketch, "E89", {"start": v(28, 12.25) * mm, "end": v(3, 12.25) * mm});
            skLineSegment(sketch, "E90", {"start": v(15.5, 63.5) * mm, "end": v(15.5, -39) * mm});
            skLineSegment(sketch, "E91", {"start": v(15.5, 12.25) * mm, "end": v(3, 24.75) * mm});
            skLineSegment(sketch, "E92", {"start": v(15.5, 12.25) * mm, "end": v(28, 24.75) * mm});
            skLineSegment(sketch, "E93", {"start": v(15.5, 6.25) * mm, "end": v(3, 18.75) * mm});
            skLineSegment(sketch, "E94", {"start": v(15.5, 6.25) * mm, "end": v(28, 18.75) * mm});
            skLineSegment(sketch, "E95", {"start": v(15.5, -39) * mm, "end": v(3, -26.5) * mm});
            skLineSegment(sketch, "E96", {"start": v(15.5, -39) * mm, "end": v(28, -26.5) * mm});
            skLineSegment(sketch, "E97", {"start": v(3, 63.5) * mm, "end": v(15.5, 51) * mm});
            skLineSegment(sketch, "E98", {"start": v(15.5, 51) * mm, "end": v(28, 63.5) * mm});
            skSolve(sketch);
        }
        {
            var Q0;
            {var subQ2=sQuery(id+"F16.wireOp",EDGE,"E92");Q0=makeQuery(id+"F16.imprint","IMPRINT",FACE,{"disambiguationData":[TD([[makeQuery(id+"F16.imprint","IMPRINT",EDGE,{"derivedFrom":subQ2}),1.0]])]});}
            var Q1;
            {var subQ2=sQuery(id+"F16.wireOp",EDGE,"E91");Q1=makeQuery(id+"F16.imprint","IMPRINT",FACE,{"disambiguationData":[TD([[makeQuery(id+"F16.imprint","IMPRINT",EDGE,{"derivedFrom":subQ2}),-1.0]])]});}
            var Q2;
            {var subQ5=sQuery(id+"F16.wireOp",EDGE,"E95");Q2=makeQuery(id+"F16.imprint","IMPRINT",FACE,{"disambiguationData":[TD([[makeQuery(id+"F16.imprint","IMPRINT",EDGE,{"derivedFrom":subQ5}),-1.0]])]});}
            var Q3;
            {var subQ5=sQuery(id+"F16.wireOp",EDGE,"E96");Q3=makeQuery(id+"F16.imprint","IMPRINT",FACE,{"disambiguationData":[TD([[makeQuery(id+"F16.imprint","IMPRINT",EDGE,{"derivedFrom":subQ5}),1.0]])]});}
            var Q4;
            {var subQ0=sQuery(id+"F16.wireOp",EDGE,"E89");var subQ1=sQuery(id+"F16.wireOp",EDGE,"E88.left");var subQ2=makeQuery(id+"F16.imprint","INTERSECT",VERTEX,{"derivedFrom":[subQ1,subQ0]});Q4=makeQuery(id+"F16.imprint","IMPRINT",FACE,{"disambiguationData":[TD([[makeQuery(id+"F16.imprint","IMPRINT",EDGE,{"disambiguationData":[TD([[subQ2,1.0]])],"derivedFrom":subQ1}),1.0]])]});}
            var Q5;
            {var subQ0=sQuery(id+"F16.wireOp",EDGE,"E89");var subQ1=sQuery(id+"F16.wireOp",EDGE,"E88.right");var subQ2=makeQuery(id+"F16.imprint","INTERSECT",VERTEX,{"derivedFrom":[subQ1,subQ0]});Q5=makeQuery(id+"F16.imprint","IMPRINT",FACE,{"disambiguationData":[TD([[makeQuery(id+"F16.imprint","IMPRINT",EDGE,{"disambiguationData":[TD([[subQ2,1.0]])],"derivedFrom":subQ1}),-1.0]])]});}
            extrude(context, id + "F17", {"entities" : qUnion([Q0, Q1, Q2, Q3, Q4, Q5]), "operationType" : NewBodyOperationType.REMOVE, "oppositeDirection" : true, "depth" : 2 * mm, "offsetDistance" : 25 * mm});
        }
        {
            var Q0;
            Q0=makeQuery(id+"F17.boolean.opBoolean","COPY",EDGE,{"derivedFrom":makeQuery(id+"F17.opExtrude","CAP_EDGE",EDGE,{"disambiguationData":[OSD([sQuery(id+"F16.wireOp",EDGE,"E97")])],"isStart":false})});
            var Q1;
            Q1=makeQuery(id+"F17.boolean.opBoolean","COPY",EDGE,{"derivedFrom":makeQuery(id+"F17.opExtrude","CAP_EDGE",EDGE,{"disambiguationData":[OSD([sQuery(id+"F16.wireOp",EDGE,"E98")])],"isStart":false})});
            var Q2;
            {var subQ0=sQuery(id+"F16.wireOp",EDGE,"E88.right");Q2=makeQuery(id+"F17.boolean.opBoolean","COPY",EDGE,{"derivedFrom":makeQuery(id+"F17.opExtrude","CAP_EDGE",EDGE,{"disambiguationData":[OSD([subQ0]),TDD([makeQuery(id+"F16.imprint","IMPRINT",EDGE,{"disambiguationData":[TD([[makeQuery(id+"F16.imprint","INTERSECT",VERTEX,{"derivedFrom":[subQ0,sQuery(id+"F16.wireOp",EDGE,"E92")]}),1.0]])],"derivedFrom":subQ0})])],"isStart":false})});}
            var Q3;
            {var subQ0=sQuery(id+"F16.wireOp",EDGE,"E88.left");Q3=makeQuery(id+"F17.boolean.opBoolean","COPY",EDGE,{"derivedFrom":makeQuery(id+"F17.opExtrude","CAP_EDGE",EDGE,{"disambiguationData":[OSD([subQ0]),TDD([makeQuery(id+"F16.imprint","IMPRINT",EDGE,{"disambiguationData":[TD([[makeQuery(id+"F16.imprint","INTERSECT",VERTEX,{"derivedFrom":[subQ0,sQuery(id+"F16.wireOp",EDGE,"E91")]}),1.0]])],"derivedFrom":subQ0})])],"isStart":false})});}
            var Q4;
            Q4=makeQuery(id+"F17.boolean.opBoolean","COPY",EDGE,{"derivedFrom":makeQuery(id+"F17.opExtrude","CAP_EDGE",EDGE,{"disambiguationData":[OSD([sQuery(id+"F16.wireOp",EDGE,"E91")])],"isStart":false})});
            var Q5;
            Q5=makeQuery(id+"F17.boolean.opBoolean","COPY",EDGE,{"derivedFrom":makeQuery(id+"F17.opExtrude","CAP_EDGE",EDGE,{"disambiguationData":[OSD([sQuery(id+"F16.wireOp",EDGE,"E92")])],"isStart":false})});
            var Q6;
            Q6=makeQuery(id+"F17.boolean.opBoolean","COPY",EDGE,{"derivedFrom":makeQuery(id+"F17.opExtrude","CAP_EDGE",EDGE,{"disambiguationData":[OSD([sQuery(id+"F16.wireOp",EDGE,"E93")])],"isStart":false})});
            var Q7;
            Q7=makeQuery(id+"F17.boolean.opBoolean","COPY",EDGE,{"derivedFrom":makeQuery(id+"F17.opExtrude","CAP_EDGE",EDGE,{"disambiguationData":[OSD([sQuery(id+"F16.wireOp",EDGE,"E94")])],"isStart":false})});
            var Q8;
            {var subQ0=sQuery(id+"F16.wireOp",EDGE,"E88.left");var subQ1=makeQuery(id+"F16.imprint","INTERSECT",VERTEX,{"derivedFrom":[subQ0,sQuery(id+"F16.wireOp",EDGE,"E89")]});Q8=makeQuery(id+"F17.boolean.opBoolean","COPY",EDGE,{"derivedFrom":makeQuery(id+"F17.opExtrude","CAP_EDGE",EDGE,{"disambiguationData":[OSD([subQ0]),TDD([makeQuery(id+"F16.imprint","IMPRINT",EDGE,{"disambiguationData":[TD([[subQ1,1.0]])],"derivedFrom":subQ0}),makeQuery(id+"F16.imprint","IMPRINT",EDGE,{"disambiguationData":[TD([[subQ1,-1.0]])],"derivedFrom":subQ0})])],"isStart":false})});}
            var Q9;
            {var subQ0=sQuery(id+"F16.wireOp",EDGE,"E88.right");var subQ1=makeQuery(id+"F16.imprint","INTERSECT",VERTEX,{"derivedFrom":[subQ0,sQuery(id+"F16.wireOp",EDGE,"E89")]});Q9=makeQuery(id+"F17.boolean.opBoolean","COPY",EDGE,{"derivedFrom":makeQuery(id+"F17.opExtrude","CAP_EDGE",EDGE,{"disambiguationData":[OSD([subQ0]),TDD([makeQuery(id+"F16.imprint","IMPRINT",EDGE,{"disambiguationData":[TD([[subQ1,1.0]])],"derivedFrom":subQ0}),makeQuery(id+"F16.imprint","IMPRINT",EDGE,{"disambiguationData":[TD([[subQ1,-1.0]])],"derivedFrom":subQ0})])],"isStart":false})});}
            var Q10;
            Q10=makeQuery(id+"F17.boolean.opBoolean","COPY",EDGE,{"derivedFrom":makeQuery(id+"F17.opExtrude","CAP_EDGE",EDGE,{"disambiguationData":[OSD([sQuery(id+"F16.wireOp",EDGE,"E96")])],"isStart":false})});
            var Q11;
            Q11=makeQuery(id+"F17.boolean.opBoolean","COPY",EDGE,{"derivedFrom":makeQuery(id+"F17.opExtrude","CAP_EDGE",EDGE,{"disambiguationData":[OSD([sQuery(id+"F16.wireOp",EDGE,"E95")])],"isStart":false})});
            chamfer(context, id + "F18", {"entities" : qUnion([Q0, Q1, Q2, Q3, Q4, Q5, Q6, Q7, Q8, Q9, Q10, Q11]), "width" : 2 * mm, "tangentPropagation" : true});
        }
        {
            var Q0;
            {var subQ0=sQuery(id+"F11.wireOp",EDGE,"E85");var subQ1=sQuery(id+"F11.wireOp",EDGE,"E70.top");var subQ2=makeQuery(id+"F11.imprint","INTERSECT",VERTEX,{"derivedFrom":[subQ1,subQ0]});Q0=makeQuery(id+"F11.imprint","IMPRINT",FACE,{"disambiguationData":[TD([[makeQuery(id+"F11.imprint","IMPRINT",EDGE,{"disambiguationData":[TD([[subQ2,-1.0]])],"derivedFrom":subQ1}),1.0]])]});}
            var Q1;
            {var subQ0=sQuery(id+"F11.wireOp",EDGE,"E77.right");var subQ1=sQuery(id+"F11.wireOp",EDGE,"E70.top");var subQ2=makeQuery(id+"F11.imprint","INTERSECT",VERTEX,{"derivedFrom":[subQ1,subQ0]});Q1=makeQuery(id+"F11.imprint","IMPRINT",FACE,{"disambiguationData":[TD([[makeQuery(id+"F11.imprint","IMPRINT",EDGE,{"disambiguationData":[TD([[subQ2,-1.0]])],"derivedFrom":subQ1}),1.0]])]});}
            var Q2;
            {var subQ0=sQuery(id+"F11.wireOp",EDGE,"E77.right");var subQ1=sQuery(id+"F11.wireOp",EDGE,"E70.top");var subQ2=makeQuery(id+"F11.imprint","INTERSECT",VERTEX,{"derivedFrom":[subQ1,subQ0]});Q2=makeQuery(id+"F11.imprint","IMPRINT",FACE,{"disambiguationData":[TD([[makeQuery(id+"F11.imprint","IMPRINT",EDGE,{"disambiguationData":[TD([[subQ2,-1.0]])],"derivedFrom":subQ1}),-1.0]])]});}
            var Q3;
            {var subQ1=sQuery(id+"F11.wireOp",EDGE,"E70.top");var subQ8=sQuery(id+"F11.wireOp",EDGE,"E85");var subQ11=makeQuery(id+"F11.imprint","INTERSECT",VERTEX,{"derivedFrom":[subQ1,subQ8]});Q3=makeQuery(id+"F11.imprint","IMPRINT",FACE,{"disambiguationData":[TD([[makeQuery(id+"F11.imprint","IMPRINT",EDGE,{"disambiguationData":[TD([[subQ11,-1.0]])],"derivedFrom":subQ1}),-1.0]])]});}
            var Q4;
            {var subQ0=sQuery(id+"F11.wireOp",EDGE,"E78");Q4=makeQuery(id+"F11.imprint","IMPRINT",FACE,{"disambiguationData":[TD([[makeQuery(id+"F11.imprint","IMPRINT",EDGE,{"derivedFrom":subQ0}),1.0]])]});}
            var Q5;
            {var subQ0=sQuery(id+"F11.wireOp",EDGE,"E77.right");var subQ1=sQuery(id+"F11.wireOp",EDGE,"E71.top");var subQ2=makeQuery(id+"F11.imprint","INTERSECT",VERTEX,{"derivedFrom":[subQ1,subQ0]});Q5=makeQuery(id+"F11.imprint","IMPRINT",FACE,{"disambiguationData":[TD([[makeQuery(id+"F11.imprint","IMPRINT",EDGE,{"disambiguationData":[TD([[subQ2,-1.0]])],"derivedFrom":subQ1}),-1.0]])]});}
            var Q6;
            {var subQ0=sQuery(id+"F11.wireOp",EDGE,"E82");Q6=makeQuery(id+"F11.imprint","IMPRINT",FACE,{"disambiguationData":[TD([[makeQuery(id+"F11.imprint","IMPRINT",EDGE,{"derivedFrom":subQ0}),1.0]])]});}
            var Q7;
            {var subQ3=sQuery(id+"F11.wireOp",EDGE,"E75");var subQ6=sQuery(id+"F11.wireOp",EDGE,"E77.right");var subQ8=makeQuery(id+"F11.imprint","INTERSECT",VERTEX,{"derivedFrom":[subQ3,subQ6]});Q7=makeQuery(id+"F11.imprint","IMPRINT",FACE,{"disambiguationData":[TD([[makeQuery(id+"F11.imprint","IMPRINT",EDGE,{"disambiguationData":[TD([[subQ8,-1.0]])],"derivedFrom":subQ3}),-1.0]])]});}
            var Q8;
            {var subQ0=sQuery(id+"F11.wireOp",EDGE,"E80");var subQ1=sQuery(id+"F11.wireOp",EDGE,"E75");var subQ2=makeQuery(id+"F11.imprint","INTERSECT",VERTEX,{"derivedFrom":[subQ1,subQ0]});Q8=makeQuery(id+"F11.imprint","IMPRINT",FACE,{"disambiguationData":[TD([[makeQuery(id+"F11.imprint","IMPRINT",EDGE,{"disambiguationData":[TD([[subQ2,-1.0]])],"derivedFrom":subQ1}),1.0]])]});}
            var Q9;
            {var subQ0=sQuery(id+"F11.wireOp",EDGE,"E77.right");var subQ1=sQuery(id+"F11.wireOp",EDGE,"E75");var subQ2=makeQuery(id+"F11.imprint","INTERSECT",VERTEX,{"derivedFrom":[subQ1,subQ0]});Q9=makeQuery(id+"F11.imprint","IMPRINT",FACE,{"disambiguationData":[TD([[makeQuery(id+"F11.imprint","IMPRINT",EDGE,{"disambiguationData":[TD([[subQ2,-1.0]])],"derivedFrom":subQ1}),1.0]])]});}
            extrude(context, id + "F19", {"entities" : qUnion([Q0, Q1, Q2, Q3, Q4, Q5, Q6, Q7, Q8, Q9]), "operationType" : NewBodyOperationType.REMOVE, "oppositeDirection" : true, "depth" : 2 * mm, "offsetDistance" : 25 * mm});
        }
        {
            var Q0;
            {var subQ0=sQuery(id+"F11.wireOp",EDGE,"E77.right");var subQ1=makeQuery(id+"F11.imprint","INTERSECT",VERTEX,{"derivedFrom":[sQuery(id+"F11.wireOp",EDGE,"E70.top"),subQ0]});Q0=makeQuery(id+"F19.boolean.opBoolean","COPY",EDGE,{"derivedFrom":makeQuery(id+"F19.opExtrude","CAP_EDGE",EDGE,{"disambiguationData":[OSD([subQ0]),TDD([makeQuery(id+"F11.imprint","IMPRINT",EDGE,{"disambiguationData":[TD([[makeQuery(id+"F11.imprint","INTERSECT",VERTEX,{"derivedFrom":[subQ0,sQuery(id+"F11.wireOp",EDGE,"E79")]}),-1.0]])],"derivedFrom":subQ0}),makeQuery(id+"F11.imprint","IMPRINT",EDGE,{"disambiguationData":[TD([[subQ1,1.0]])],"derivedFrom":subQ0}),makeQuery(id+"F11.imprint","IMPRINT",EDGE,{"disambiguationData":[TD([[subQ1,-1.0]])],"derivedFrom":subQ0})])],"isStart":false})});}
            var Q1;
            Q1=makeQuery(id+"F19.boolean.opBoolean","COPY",EDGE,{"derivedFrom":makeQuery(id+"F19.opExtrude","CAP_EDGE",EDGE,{"disambiguationData":[OSD([sQuery(id+"F11.wireOp",EDGE,"E85")])],"isStart":false})});
            var Q2;
            Q2=makeQuery(id+"F19.boolean.opBoolean","COPY",EDGE,{"derivedFrom":makeQuery(id+"F19.opExtrude","CAP_EDGE",EDGE,{"disambiguationData":[OSD([sQuery(id+"F11.wireOp",EDGE,"E86")])],"isStart":false})});
            var Q3;
            {var subQ0=sQuery(id+"F11.wireOp",EDGE,"E77.left");var subQ1=makeQuery(id+"F11.imprint","INTERSECT",VERTEX,{"derivedFrom":[sQuery(id+"F11.wireOp",EDGE,"E70.top"),subQ0]});Q3=makeQuery(id+"F19.boolean.opBoolean","COPY",EDGE,{"derivedFrom":makeQuery(id+"F19.opExtrude","CAP_EDGE",EDGE,{"disambiguationData":[OSD([subQ0]),TDD([makeQuery(id+"F11.imprint","IMPRINT",EDGE,{"disambiguationData":[TD([[makeQuery(id+"F11.imprint","INTERSECT",VERTEX,{"derivedFrom":[subQ0,sQuery(id+"F11.wireOp",EDGE,"E78")]}),-1.0]])],"derivedFrom":subQ0}),makeQuery(id+"F11.imprint","IMPRINT",EDGE,{"disambiguationData":[TD([[subQ1,1.0]])],"derivedFrom":subQ0}),makeQuery(id+"F11.imprint","IMPRINT",EDGE,{"disambiguationData":[TD([[subQ1,-1.0]])],"derivedFrom":subQ0})])],"isStart":false})});}
            var Q4;
            Q4=makeQuery(id+"F19.boolean.opBoolean","COPY",EDGE,{"derivedFrom":makeQuery(id+"F19.opExtrude","CAP_EDGE",EDGE,{"disambiguationData":[OSD([sQuery(id+"F11.wireOp",EDGE,"E79")])],"isStart":false})});
            var Q5;
            Q5=makeQuery(id+"F19.boolean.opBoolean","COPY",EDGE,{"derivedFrom":makeQuery(id+"F19.opExtrude","CAP_EDGE",EDGE,{"disambiguationData":[OSD([sQuery(id+"F11.wireOp",EDGE,"E78")])],"isStart":false})});
            var Q6;
            Q6=makeQuery(id+"F19.boolean.opBoolean","COPY",EDGE,{"derivedFrom":makeQuery(id+"F19.opExtrude","CAP_EDGE",EDGE,{"disambiguationData":[OSD([sQuery(id+"F11.wireOp",EDGE,"E80")])],"isStart":false})});
            var Q7;
            Q7=makeQuery(id+"F19.boolean.opBoolean","COPY",EDGE,{"derivedFrom":makeQuery(id+"F19.opExtrude","CAP_EDGE",EDGE,{"disambiguationData":[OSD([sQuery(id+"F11.wireOp",EDGE,"E81")])],"isStart":false})});
            var Q8;
            {var subQ0=sQuery(id+"F11.wireOp",EDGE,"E77.right");Q8=makeQuery(id+"F19.boolean.opBoolean","COPY",EDGE,{"derivedFrom":makeQuery(id+"F19.opExtrude","CAP_EDGE",EDGE,{"disambiguationData":[OSD([subQ0]),TDD([makeQuery(id+"F11.imprint","IMPRINT",EDGE,{"disambiguationData":[TD([[makeQuery(id+"F11.imprint","INTERSECT",VERTEX,{"derivedFrom":[subQ0,sQuery(id+"F11.wireOp",EDGE,"E83")]}),-1.0]])],"derivedFrom":subQ0}),makeQuery(id+"F11.imprint","IMPRINT",EDGE,{"disambiguationData":[TD([[makeQuery(id+"F11.imprint","INTERSECT",VERTEX,{"derivedFrom":[subQ0,sQuery(id+"F11.wireOp",EDGE,"E81")]}),1.0]])],"derivedFrom":subQ0})])],"isStart":false})});}
            var Q9;
            {var subQ0=sQuery(id+"F11.wireOp",EDGE,"E77.left");Q9=makeQuery(id+"F19.boolean.opBoolean","COPY",EDGE,{"derivedFrom":makeQuery(id+"F19.opExtrude","CAP_EDGE",EDGE,{"disambiguationData":[OSD([subQ0]),TDD([makeQuery(id+"F11.imprint","IMPRINT",EDGE,{"disambiguationData":[TD([[makeQuery(id+"F11.imprint","INTERSECT",VERTEX,{"derivedFrom":[subQ0,sQuery(id+"F11.wireOp",EDGE,"E82")]}),-1.0]])],"derivedFrom":subQ0}),makeQuery(id+"F11.imprint","IMPRINT",EDGE,{"disambiguationData":[TD([[makeQuery(id+"F11.imprint","INTERSECT",VERTEX,{"derivedFrom":[subQ0,sQuery(id+"F11.wireOp",EDGE,"E80")]}),1.0]])],"derivedFrom":subQ0})])],"isStart":false})});}
            var Q10;
            Q10=makeQuery(id+"F19.boolean.opBoolean","COPY",EDGE,{"derivedFrom":makeQuery(id+"F19.opExtrude","CAP_EDGE",EDGE,{"disambiguationData":[OSD([sQuery(id+"F11.wireOp",EDGE,"E82")])],"isStart":false})});
            var Q11;
            Q11=makeQuery(id+"F19.boolean.opBoolean","COPY",EDGE,{"derivedFrom":makeQuery(id+"F19.opExtrude","CAP_EDGE",EDGE,{"disambiguationData":[OSD([sQuery(id+"F11.wireOp",EDGE,"E83")])],"isStart":false})});
            chamfer(context, id + "F20", {"entities" : qUnion([Q0, Q1, Q2, Q3, Q4, Q5, Q6, Q7, Q8, Q9, Q10, Q11]), "width" : 2 * mm, "tangentPropagation" : true});
        }
    });
